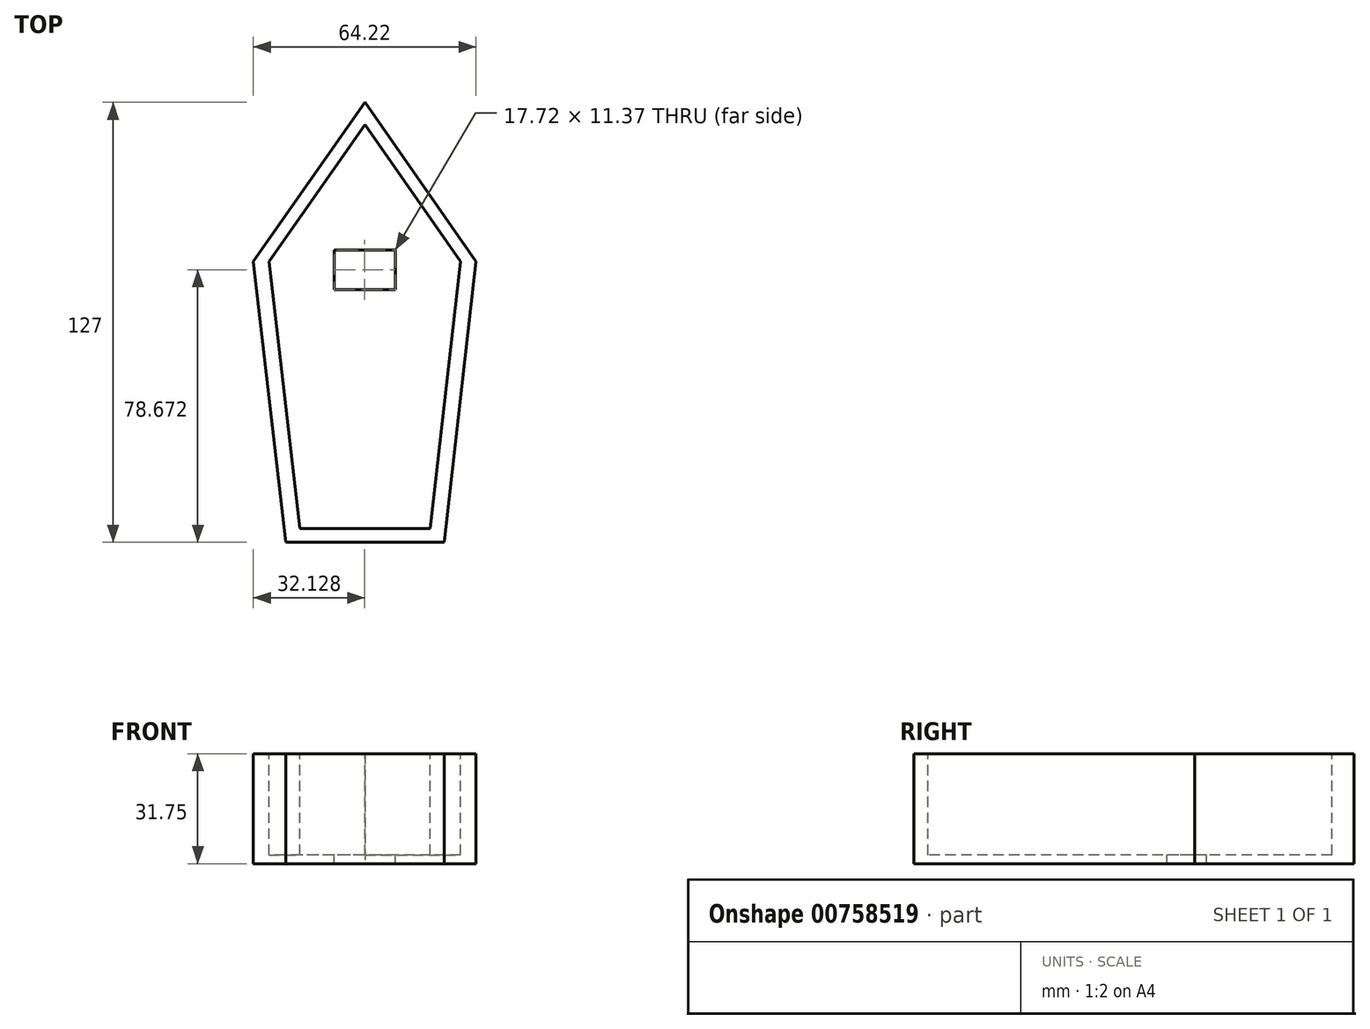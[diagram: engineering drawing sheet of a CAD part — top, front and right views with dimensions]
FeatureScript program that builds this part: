
annotation { "Feature Type Name" : "Feature", "Feature Type Description" : "" }
export const myFeature = defineFeature(function(context is Context, id is Id, definition is map)
    precondition{}
    {
        {
            var Q0;
            Q0=qCreatedBy(makeId("Top.planeOp"),FACE);
            var sketch = newSketch(context, id + "F0", { "sketchPlane" : qUnion([Q0])});
            skLineSegment(sketch, "E0.bottom", {"start": v(-25.06, 48.98) * mm, "end": v(20.66, 48.98) * mm});
            skLineSegment(sketch, "E0.top", {"start": v(-25.06, -45) * mm, "end": v(20.66, -45) * mm});
            skLineSegment(sketch, "E0.left", {"start": v(-25.06, 48.98) * mm, "end": v(-25.06, -45) * mm});
            skLineSegment(sketch, "E0.right", {"start": v(20.66, 48.98) * mm, "end": v(20.66, -45) * mm});
            skLineSegment(sketch, "E1", {"start": v(-2.2, -45) * mm, "end": v(-2.2, 82) * mm});
            skLineSegment(sketch, "E2", {"start": v(-2.2, 82) * mm, "end": v(-34.44, 36.02) * mm});
            skLineSegment(sketch, "E3", {"start": v(-34.44, 36.02) * mm, "end": v(-25.06, -45) * mm});
            skLineSegment(sketch, "E4", {"start": v(-2.2, 82) * mm, "end": v(29.78, 36.02) * mm});
            skLineSegment(sketch, "E5", {"start": v(29.78, 36.02) * mm, "end": v(20.66, -45) * mm});
            skSolve(sketch);
        }
        {
            var Q0;
            Q0 = qSketchRegion(id + "F0", true);
            extrude(context, id + "F1", {"entities" : qUnion([Q0]), "depth" : 31.75 * mm, "offsetDistance" : 25.4 * mm});
        }
        {
            var Q0;
            Q0=makeQuery(id+"F1.opExtrude","CAP_FACE",FACE,{"disambiguationData":[OSD([sQuery(id+"F0.wireOp",EDGE,"E0.top"),sQuery(id+"F0.wireOp",EDGE,"E2"),sQuery(id+"F0.wireOp",EDGE,"E3"),sQuery(id+"F0.wireOp",EDGE,"E4"),sQuery(id+"F0.wireOp",EDGE,"E5")])],"isStart":false});
            var sketch = newSketch(context, id + "F2", { "sketchPlane" : qUnion([Q0])});
            skLineSegment(sketch, "E6", {"start": v(-2.2, 82) * mm, "end": v(-2.2, 75.55) * mm});
            skLineSegment(sketch, "E7", {"start": v(-2.2, 75.55) * mm, "end": v(-29.92, 36.02) * mm});
            skLineSegment(sketch, "E8", {"start": v(-29.92, 36.02) * mm, "end": v(-21, -41.01) * mm});
            skLineSegment(sketch, "E9", {"start": v(-2.2, 75.55) * mm, "end": v(25.3, 36.02) * mm});
            skLineSegment(sketch, "E10", {"start": v(25.3, 36.02) * mm, "end": v(16.62, -41.01) * mm});
            skLineSegment(sketch, "E11", {"start": v(16.62, -41.01) * mm, "end": v(-21, -41.01) * mm});
            skSolve(sketch);
        }
        {
            var Q0;
            Q0=makeQuery(id+"F2.imprint","IMPRINT",FACE,{"disambiguationData":[TD([[makeQuery(id+"F2.imprint","IMPRINT",EDGE,{"derivedFrom":sQuery(id+"F2.wireOp",EDGE,"E7")}),1.0]])]});
            extrude(context, id + "F3", {"entities" : qUnion([Q0]), "operationType" : NewBodyOperationType.REMOVE, "oppositeDirection" : true, "depth" : 29.2 * mm, "offsetDistance" : 25.4 * mm});
        }
        {
            var Q0;
            Q0=makeQuery(id+"F3.boolean.opBoolean","COPY",FACE,{"derivedFrom":makeQuery(id+"F3.opExtrude","CAP_FACE",FACE,{"disambiguationData":[OSD([sQuery(id+"F2.wireOp",EDGE,"E7"),sQuery(id+"F2.wireOp",EDGE,"E8"),sQuery(id+"F2.wireOp",EDGE,"E9"),sQuery(id+"F2.wireOp",EDGE,"E10"),sQuery(id+"F2.wireOp",EDGE,"E11")])],"isStart":false})});
            var sketch = newSketch(context, id + "F4", { "sketchPlane" : qUnion([Q0])});
            skLineSegment(sketch, "E12", {"start": v(-2.2, 75.55) * mm, "end": v(-2.2, 39.36) * mm});
            skLineSegment(sketch, "E13", {"start": v(-2.2, 39.36) * mm, "end": v(-11.17, 39.36) * mm});
            skLineSegment(sketch, "E14.bottom", {"start": v(-11.17, 39.36) * mm, "end": v(6.55, 39.36) * mm});
            skLineSegment(sketch, "E14.top", {"start": v(-11.17, 27.98) * mm, "end": v(6.55, 27.98) * mm});
            skLineSegment(sketch, "E14.left", {"start": v(-11.17, 39.36) * mm, "end": v(-11.17, 27.98) * mm});
            skLineSegment(sketch, "E14.right", {"start": v(6.55, 39.36) * mm, "end": v(6.55, 27.98) * mm});
            skSolve(sketch);
        }
        {
            var Q0;
            Q0=makeQuery(id+"F4.imprint","IMPRINT",FACE,{"disambiguationData":[TD([[makeQuery(id+"F4.imprint","IMPRINT",EDGE,{"derivedFrom":sQuery(id+"F4.wireOp",EDGE,"E14.top")}),1.0]])]});
            extrude(context, id + "F5", {"entities" : qUnion([Q0]), "operationType" : NewBodyOperationType.REMOVE, "oppositeDirection" : true, "depth" : 25.4 * mm, "offsetDistance" : 25.4 * mm});
        }
    });
